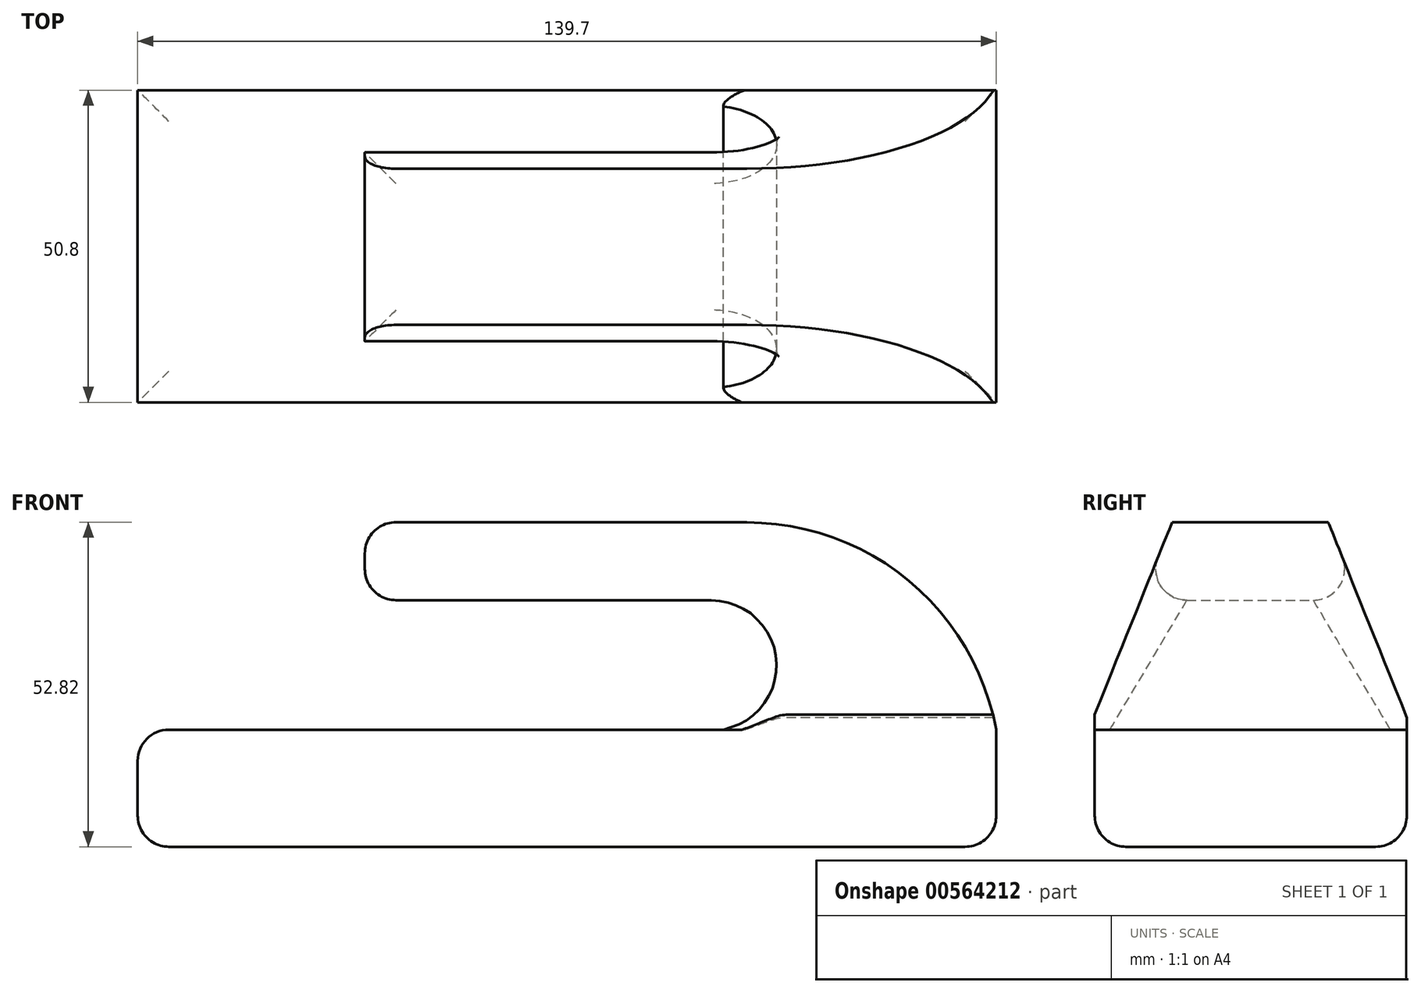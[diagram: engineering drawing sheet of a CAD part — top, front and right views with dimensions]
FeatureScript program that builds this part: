
annotation { "Feature Type Name" : "Feature", "Feature Type Description" : "" }
export const myFeature = defineFeature(function(context is Context, id is Id, definition is map)
    precondition{}
    {
        {
            var Q0;
            Q0=qCreatedBy(makeId("Front.planeOp"),FACE);
            var sketch = newSketch(context, id + "F0", { "sketchPlane" : qUnion([Q0])});
            skLineSegment(sketch, "E0.top", {"start": v(-62.26, -21) * mm, "end": v(77.44, -21) * mm});
            skLineSegment(sketch, "E0.left", {"start": v(-62.26, -1.96) * mm, "end": v(-62.26, -21) * mm});
            skLineSegment(sketch, "E0.right", {"start": v(77.44, -1.96) * mm, "end": v(77.44, -21) * mm});
            skLineSegment(sketch, "E1", {"start": v(-25.3, 31.81) * mm, "end": v(36.87, 31.81) * mm});
            skArc(sketch, "E2", {"start": v(77.44, -1.96) * mm, "mid": v(63.26, 22.26) * mm, "end": v(36.87, 31.81) * mm});
            skLineSegment(sketch, "E3", {"start": v(-25.3, 31.81) * mm, "end": v(-25.3, 19.11) * mm});
            skLineSegment(sketch, "E4", {"start": v(-25.3, 19.11) * mm, "end": v(31.09, 19.11) * mm});
            skArc(sketch, "E5", {"start": v(33.02, -1.96) * mm, "mid": v(41.67, 9.46) * mm, "end": v(31.09, 19.11) * mm});
            skLineSegment(sketch, "E6", {"start": v(-62.26, -1.96) * mm, "end": v(33.02, -1.96) * mm});
            skSolve(sketch);
        }
        {
            var Q0;
            Q0 = qSketchRegion(id + "F0", true);
            extrude(context, id + "F1", {"entities" : qUnion([Q0]), "depth" : 50.8 * mm, "offsetDistance" : 25.4 * mm});
        }
        {
            var Q0;
            Q0=qCreatedBy(makeId("Right.planeOp"),FACE);
            var sketch = newSketch(context, id + "F2", { "sketchPlane" : qUnion([Q0])});
            skLineSegment(sketch, "E7", {"start": v(-12.8, 31.81) * mm, "end": v(0, 0) * mm});
            skLineSegment(sketch, "E8", {"start": v(0, 31.81) * mm, "end": v(-12.8, 31.81) * mm});
            skLineSegment(sketch, "E9", {"start": v(-38.2, 31.81) * mm, "end": v(-50.99, 0) * mm});
            skLineSegment(sketch, "E10", {"start": v(-50.99, 31.81) * mm, "end": v(-38.2, 31.81) * mm});
            skLineSegment(sketch, "E11", {"start": v(-50.99, 0) * mm, "end": v(-50.99, 31.81) * mm});
            skLineSegment(sketch, "E12", {"start": v(0, 31.81) * mm, "end": v(0, 0) * mm});
            skSolve(sketch);
        }
        {
            var Q0;
            Q0 = qSketchRegion(id + "F2", true);
            extrude(context, id + "F3", {"entities" : qUnion([Q0]), "operationType" : NewBodyOperationType.REMOVE, "oppositeDirection" : true, "depth" : -152.4 * mm, "offsetDistance" : 25.4 * mm});
        }
        {
            var Q0;
            Q0 = qSketchRegion(id + "F2", true);
            extrude(context, id + "F4", {"entities" : qUnion([Q0]), "operationType" : NewBodyOperationType.REMOVE, "oppositeDirection" : true, "depth" : 50.8 * mm, "offsetDistance" : 25.4 * mm});
        }
        {
            var Q0;
            {var subQ0=sQuery(id+"F2.wireOp",EDGE,"E8");var subQ1=sQuery(id+"F2.wireOp",EDGE,"E7");Q0=makeQuery(id+"F4.boolean.opBoolean","MERGE",EDGE,{"derivedFrom":[makeQuery(id+"F3.boolean.opBoolean","COPY",EDGE,{"derivedFrom":makeQuery(id+"F3.opExtrude","SWEPT_EDGE",EDGE,{"disambiguationData":[OSD([subQ1,subQ0])]})}),makeQuery(id+"F4.opExtrude","SWEPT_EDGE",EDGE,{"disambiguationData":[OSD([subQ1,subQ0])]})]});}
            var Q1;
            {var subQ0=sQuery(id+"F2.wireOp",EDGE,"E10");var subQ1=sQuery(id+"F2.wireOp",EDGE,"E9");Q1=makeQuery(id+"F4.boolean.opBoolean","MERGE",EDGE,{"derivedFrom":[makeQuery(id+"F3.boolean.opBoolean","COPY",EDGE,{"derivedFrom":makeQuery(id+"F3.opExtrude","SWEPT_EDGE",EDGE,{"disambiguationData":[OSD([subQ1,subQ0])]})}),makeQuery(id+"F4.opExtrude","SWEPT_EDGE",EDGE,{"disambiguationData":[OSD([subQ1,subQ0])]})]});}
            var Q2;
            Q2=makeQuery(id+"F4.boolean.opBoolean","INTERSECT",EDGE,{"derivedFrom":[makeQuery(id+"F1.opExtrude","SWEPT_FACE",FACE,{"disambiguationData":[OSD([sQuery(id+"F0.wireOp",EDGE,"E4")])]}),makeQuery(id+"F4.opExtrude","SWEPT_FACE",FACE,{"disambiguationData":[OSD([sQuery(id+"F2.wireOp",EDGE,"E7")])]})]});
            var Q3;
            Q3=makeQuery(id+"F1.opExtrude","SWEPT_EDGE",EDGE,{"disambiguationData":[OSD([sQuery(id+"F0.wireOp",EDGE,"E3"),sQuery(id+"F0.wireOp",EDGE,"E4")])]});
            var Q4;
            Q4=makeQuery(id+"F4.boolean.opBoolean","INTERSECT",EDGE,{"derivedFrom":[makeQuery(id+"F1.opExtrude","SWEPT_FACE",FACE,{"disambiguationData":[OSD([sQuery(id+"F0.wireOp",EDGE,"E4")])]}),makeQuery(id+"F4.opExtrude","SWEPT_FACE",FACE,{"disambiguationData":[OSD([sQuery(id+"F2.wireOp",EDGE,"E9")])]})]});
            fillet(context, id + "F5", {"entities" : qUnion([Q0, Q1, Q2, Q3, Q4]), "radius" : 5.08 * mm, "tangentPropagation" : true, "allowEdgeOverflow" : false});
        }
        {
            var Q0;
            Q0=makeQuery(id+"F1.opExtrude","CAP_EDGE",EDGE,{"disambiguationData":[OSD([sQuery(id+"F0.wireOp",EDGE,"E0.top")])],"isStart":false});
            var Q1;
            Q1=makeQuery(id+"F1.opExtrude","CAP_EDGE",EDGE,{"disambiguationData":[OSD([sQuery(id+"F0.wireOp",EDGE,"E0.top")])],"isStart":true});
            var Q2;
            Q2=makeQuery(id+"F1.opExtrude","SWEPT_EDGE",EDGE,{"disambiguationData":[OSD([sQuery(id+"F0.wireOp",EDGE,"E0.top"),sQuery(id+"F0.wireOp",EDGE,"E0.left")])]});
            var Q3;
            Q3=makeQuery(id+"F1.opExtrude","SWEPT_EDGE",EDGE,{"disambiguationData":[OSD([sQuery(id+"F0.wireOp",EDGE,"E0.top"),sQuery(id+"F0.wireOp",EDGE,"E0.right")])]});
            var Q4;
            Q4=makeQuery(id+"F1.opExtrude","SWEPT_EDGE",EDGE,{"disambiguationData":[OSD([sQuery(id+"F0.wireOp",EDGE,"E0.left"),sQuery(id+"F0.wireOp",EDGE,"E6")])]});
            fillet(context, id + "F6", {"entities" : qUnion([Q0, Q1, Q2, Q3, Q4]), "radius" : 5.08 * mm, "tangentPropagation" : true, "allowEdgeOverflow" : false});
        }
        {
            var Q0;
            Q0=makeQuery(id+"F1.opExtrude","SWEPT_EDGE",EDGE,{"disambiguationData":[OSD([sQuery(id+"F0.wireOp",EDGE,"E1"),sQuery(id+"F0.wireOp",EDGE,"E3")])]});
            fillet(context, id + "F7", {"entities" : qUnion([Q0]), "radius" : 5.08 * mm, "tangentPropagation" : true, "allowEdgeOverflow" : false});
        }
    });
